# Revit family: Table-LAMMHULTS-ATTACH-Round_4_Legs
name_source: partatom
category: Furniture
revit_build: Autodesk Revit 2014 (Build: 20140709_2115(x64)
units: mm (PartAtom-declared; Revit-internal decimal feet)

## types (4) — shared parameters
Assembly Code = E2020
Description = *Please enter mtrl description here for use in mto*
Foot Material = Plastic - Black
Frame Material = Metal - Aluminium - Matte
Keynote = 46.B
Legs Material = Metal - Aluminium - Matte
Manufacturer = LAMMHULTS
Model = ATTACH
Table Top Material = Laminate - High Pressure - White/Grey
URL = www.lammhults.se

## per-type parameters (varying)
| type | Frame Positioning | Table Top Diameter |
| D120 Laminate broken white | 287.5 mm | 1200 mm |
| D150 Laminate broken white | 407.5 mm | 1500 mm |
| D170 Laminate broken white | 407.5 mm | 1700 mm  [stored 5.57743 ft] |
| D200 Laminate broken white | 527.5 mm | 2000 mm |

note: [stored X ft] marks values corroborated as IEEE doubles in the binary element streams (Revit-internal decimal feet)

## geometry (parser evidence)
native form markers: Blend x2, Sweep x7
no freeform markers — native parametric forms only
